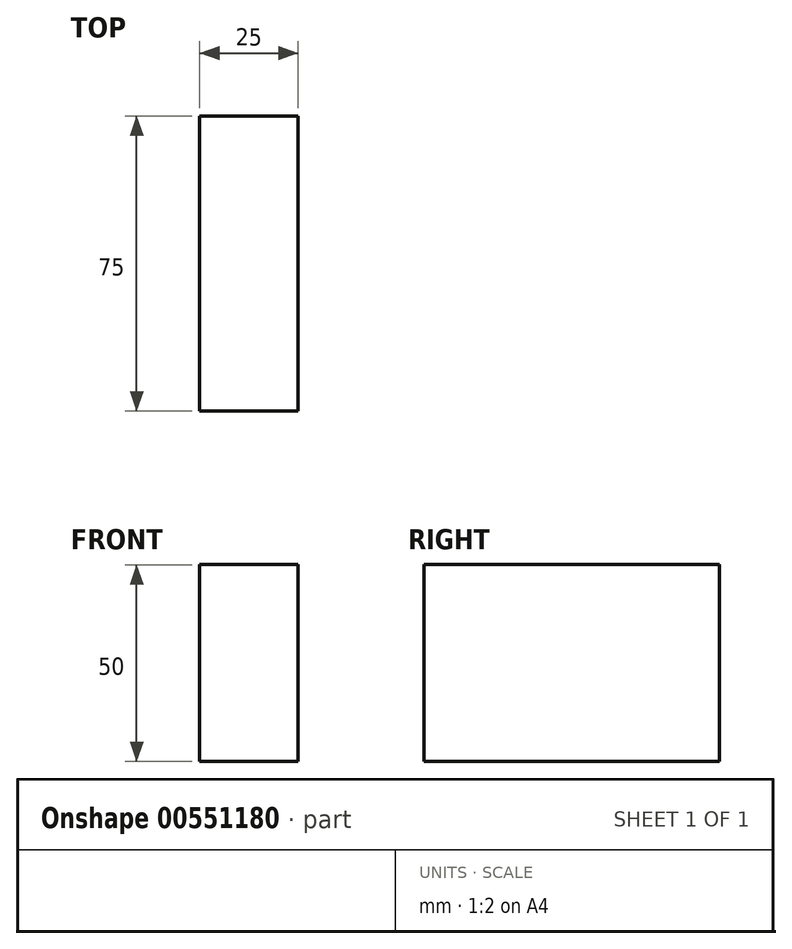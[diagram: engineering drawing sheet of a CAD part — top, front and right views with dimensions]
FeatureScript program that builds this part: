
annotation { "Feature Type Name" : "Feature", "Feature Type Description" : "" }
export const myFeature = defineFeature(function(context is Context, id is Id, definition is map)
    precondition{}
    {
        {
            var Q0;
            Q0=qCreatedBy(makeId("Front.planeOp"),FACE);
            var sketch = newSketch(context, id + "F0", { "sketchPlane" : qUnion([Q0])});
            skLineSegment(sketch, "E0.bottom", {"start": v(-26.78, 47.63) * mm, "end": v(-1.78, 47.63) * mm});
            skLineSegment(sketch, "E0.top", {"start": v(-26.78, -2.37) * mm, "end": v(-1.78, -2.37) * mm});
            skLineSegment(sketch, "E0.left", {"start": v(-26.78, 47.63) * mm, "end": v(-26.78, -2.37) * mm});
            skLineSegment(sketch, "E0.right", {"start": v(-1.78, 47.63) * mm, "end": v(-1.78, -2.37) * mm});
            skSolve(sketch);
        }
        {
            var Q0;
            Q0=makeQuery(id+"F0.imprint","IMPRINT",FACE,{"disambiguationData":[TD([[makeQuery(id+"F0.imprint","IMPRINT",EDGE,{"derivedFrom":sQuery(id+"F0.wireOp",EDGE,"E0.bottom")}),-1.0]])]});
            extrude(context, id + "F1", {"entities" : qUnion([Q0]), "depth" : 75 * mm, "offsetDistance" : 25 * mm});
        }
    });
